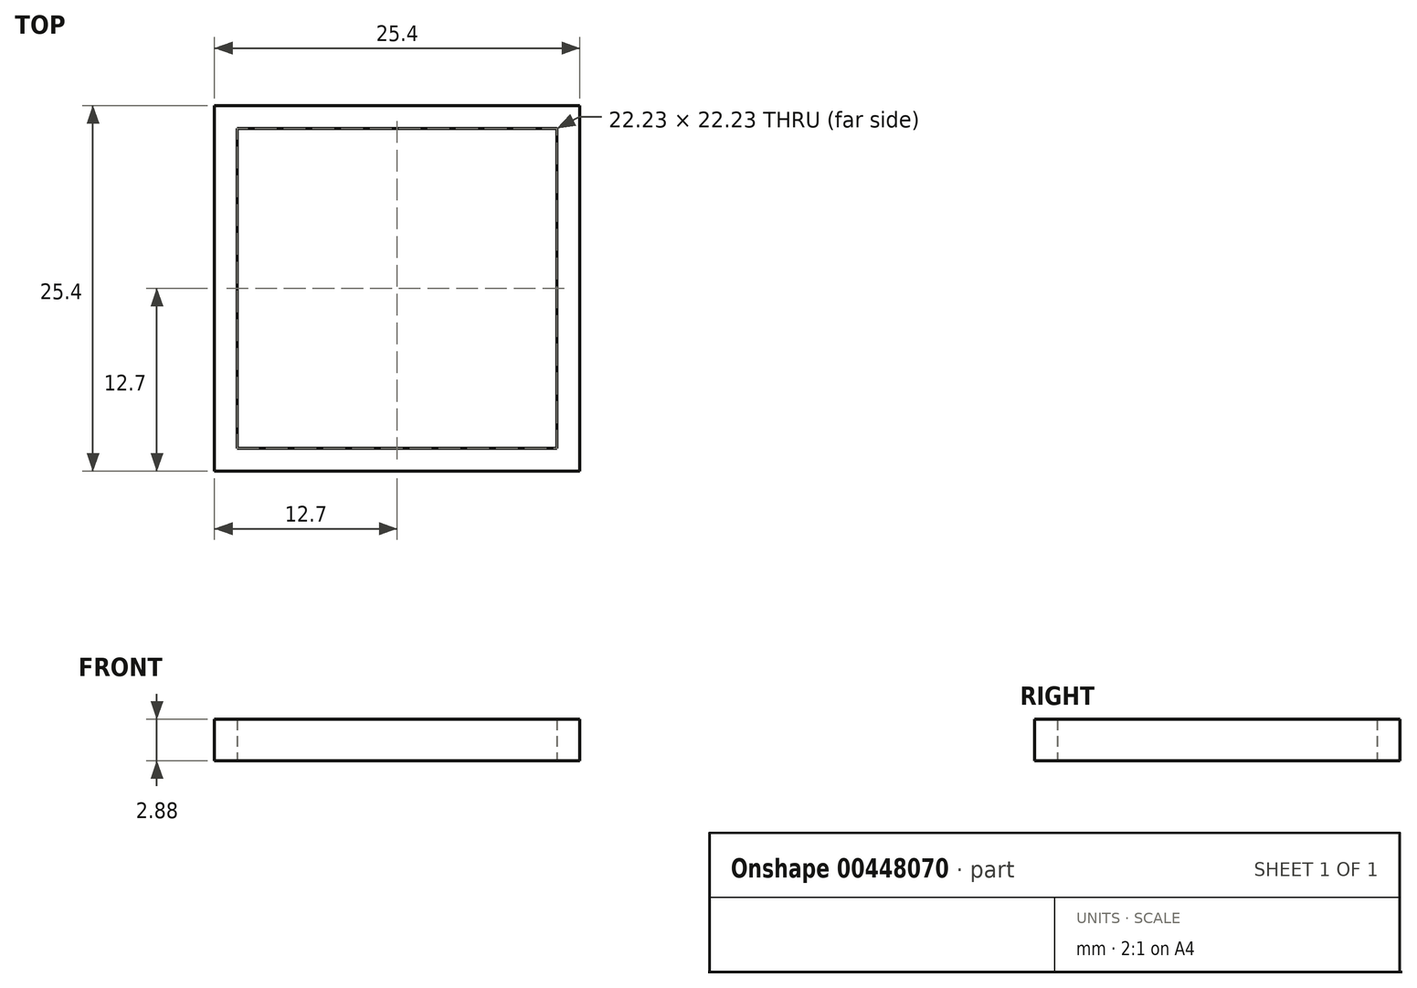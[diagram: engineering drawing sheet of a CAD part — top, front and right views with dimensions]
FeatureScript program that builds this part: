
annotation { "Feature Type Name" : "Feature", "Feature Type Description" : "" }
export const myFeature = defineFeature(function(context is Context, id is Id, definition is map)
    precondition{}
    {
        {
            assignVariable(context, id + "F0", {"name" : "SideW", "anyValue" : 2.88});
        }
        {
            var Q0;
            Q0=qCreatedBy(makeId("Top.planeOp"),FACE);
            var sketch = newSketch(context, id + "F1", { "sketchPlane" : qUnion([Q0])});
            skLineSegment(sketch, "E0.bottom", {"start": v(-12.7, 12.7) * mm, "end": v(12.7, 12.7) * mm});
            skLineSegment(sketch, "E0.top", {"start": v(-12.7, -12.7) * mm, "end": v(12.7, -12.7) * mm});
            skLineSegment(sketch, "E0.left", {"start": v(-12.7, 12.7) * mm, "end": v(-12.7, -12.7) * mm});
            skLineSegment(sketch, "E0.right", {"start": v(12.7, 12.7) * mm, "end": v(12.7, -12.7) * mm});
            skPoint(sketch, "E0.middle", {"position": v(0, 0) * mm});
            skSolve(sketch);
        }
        {
            var Q0;
            Q0=makeQuery(id+"F1.imprint","IMPRINT",FACE,{"disambiguationData":[TD([[makeQuery(id+"F1.imprint","IMPRINT",EDGE,{"derivedFrom":sQuery(id+"F1.wireOp",EDGE,"E0.bottom")}),-1.0]])]});
            var Q1;
            Q1 = qConstructionFilter(qBodyType(qCreatedBy(id + "F1" ,EDGE), BodyType.WIRE), ConstructionObject.NO);
            extrude(context, id + "F2", {"entities" : qUnion([Q0]), "surfaceEntities" : qUnion([Q1]), "depth" : (getVariable(context, 'SideW')) * mm});
        }
        {
            var Q0;
            Q0=makeQuery(id+"F2.opExtrude","CAP_FACE",FACE,{"disambiguationData":[OSD([sQuery(id+"F1.wireOp",EDGE,"E0.bottom"),sQuery(id+"F1.wireOp",EDGE,"E0.top"),sQuery(id+"F1.wireOp",EDGE,"E0.left"),sQuery(id+"F1.wireOp",EDGE,"E0.right")])],"isStart":false});
            shell(context, id + "F3", {"entities" : qUnion([Q0]), "thickness" : 1.59 * mm});
        }
        {
            var Q0;
            Q0=makeQuery(id+"F3.opShell","OFFSET_FACE",FACE,{"disambiguationData":[OSD([sQuery(id+"F1.wireOp",EDGE,"E0.bottom"),sQuery(id+"F1.wireOp",EDGE,"E0.top"),sQuery(id+"F1.wireOp",EDGE,"E0.left"),sQuery(id+"F1.wireOp",EDGE,"E0.right")])]});
            extrude(context, id + "F4", {"entities" : qUnion([Q0]), "operationType" : NewBodyOperationType.REMOVE, "endBound" : BoundingType.THROUGH_ALL, "oppositeDirection" : true, "depth" : 25.4 * mm});
        }
    });
